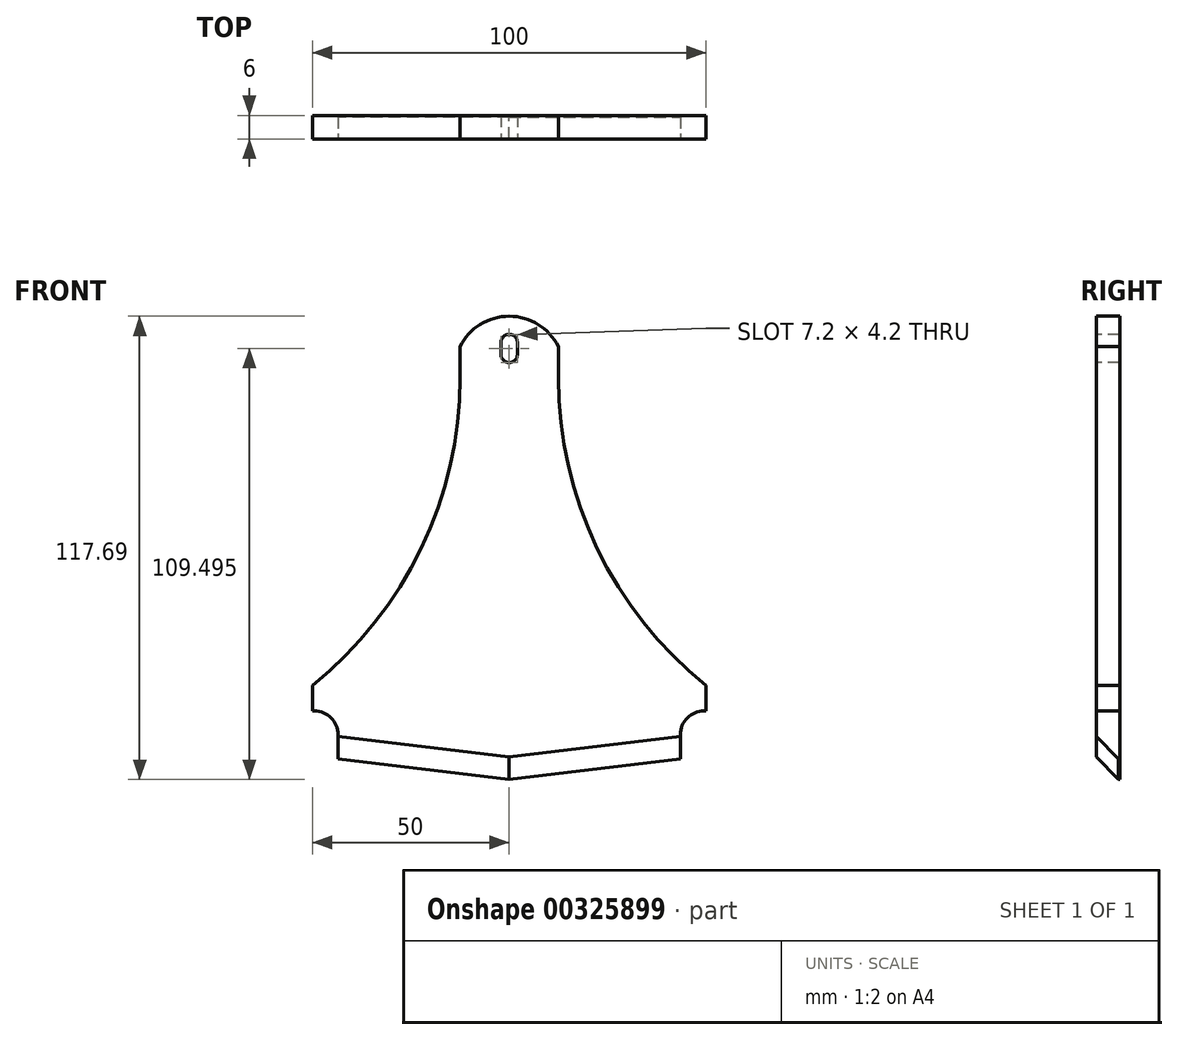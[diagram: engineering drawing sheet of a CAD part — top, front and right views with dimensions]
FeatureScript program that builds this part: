
annotation { "Feature Type Name" : "Feature", "Feature Type Description" : "" }
export const myFeature = defineFeature(function(context is Context, id is Id, definition is map)
    precondition{}
    {
        {
            var Q0;
            Q0=qCreatedBy(makeId("Front.planeOp"),FACE);
            var sketch = newSketch(context, id + "F0", { "sketchPlane" : qUnion([Q0])});
            skLineSegment(sketch, "E0", {"start": v(0, -15.28) * mm, "end": v(-43.5, -10.06) * mm});
            skLineSegment(sketch, "E1", {"start": v(0, -15.28) * mm, "end": v(0, 102.4) * mm});
            skLineSegment(sketch, "E2", {"start": v(-43.5, -10.06) * mm, "end": v(-43.5, 2.1) * mm});
            skCircle(sketch, "E3", {"center": v(0, 88.4) * mm, "radius": 14 * mm});
            skLineSegment(sketch, "E4", {"start": v(-43.5, 2.1) * mm, "end": v(-50, 2.1) * mm});
            skPoint(sketch, "E5", {"position": v(0, 102.4) * mm});
            skLineSegment(sketch, "E6", {"start": v(-12.5, 94.71) * mm, "end": v(-12.5, 8.6) * mm});
            skLineSegment(sketch, "E7", {"start": v(-50, 2.1) * mm, "end": v(-50, 8.6) * mm});
            skLineSegment(sketch, "E8", {"start": v(-50, 8.6) * mm, "end": v(-12.5, 8.6) * mm});
            skCircle(sketch, "E9", {"center": v(0, 95.71) * mm, "radius": 2.1 * mm});
            skCircle(sketch, "E10", {"center": v(0, 92.71) * mm, "radius": 2.1 * mm});
            skLineSegment(sketch, "E11", {"start": v(-2.1, 95.71) * mm, "end": v(-2.1, 92.71) * mm});
            skSolve(sketch);
        }
        {
            var Q0;
            {var subQ6=sQuery(id+"F0.wireOp",EDGE,"E0");Q0=makeQuery(id+"F0.imprint","IMPRINT",FACE,{"disambiguationData":[TD([[makeQuery(id+"F0.imprint","IMPRINT",EDGE,{"derivedFrom":subQ6}),-1.0]])]});}
            var Q1;
            {var subQ7=sQuery(id+"F0.wireOp",EDGE,"E11");Q1=makeQuery(id+"F0.imprint","IMPRINT",FACE,{"disambiguationData":[TD([[makeQuery(id+"F0.imprint","IMPRINT",EDGE,{"derivedFrom":subQ7}),-1.0]])]});}
            extrude(context, id + "F1", {"entities" : qUnion([Q0, Q1]), "oppositeDirection" : true, "depth" : 6 * mm});
        }
        {
            var Q0;
            Q0=makeQuery(id+"F1.opExtrude","SWEPT_EDGE",EDGE,{"disambiguationData":[OSD([sQuery(id+"F0.wireOp",EDGE,"E2"),sQuery(id+"F0.wireOp",EDGE,"E4")])]});
            fillet(context, id + "F2", {"entities" : qUnion([Q0]), "radius" : 6 * mm, "tangentPropagation" : true, "allowEdgeOverflow" : false});
        }
        {
            var Q0;
            Q0=makeQuery(id+"F1.opExtrude","CAP_EDGE",EDGE,{"disambiguationData":[OSD([sQuery(id+"F0.wireOp",EDGE,"E0")])],"isStart":true});
            chamfer(context, id + "F3", {"entities" : qUnion([Q0]), "chamferType" : ChamferType.TWO_OFFSETS, "width1" : 5.64 * mm, "oppositeDirection" : true, "width2" : 5.6 * mm, "tangentPropagation" : true});
        }
        {
            var Q0;
            Q0=makeQuery(id+"F1.opExtrude","SWEPT_EDGE",EDGE,{"disambiguationData":[OSD([sQuery(id+"F0.wireOp",EDGE,"E6"),sQuery(id+"F0.wireOp",EDGE,"E8")])]});
            fillet(context, id + "F4", {"entities" : qUnion([Q0]), "radius" : 100 * mm, "tangentPropagation" : true, "allowEdgeOverflow" : false});
        }
        {
            var Q0;
            Q0=makeQuery(id+"F1.opExtrude","SWEPT_BODY",BODY,{"disambiguationData":[OSD([sQuery(id+"F0.wireOp",EDGE,"E0"),sQuery(id+"F0.wireOp",EDGE,"E1"),sQuery(id+"F0.wireOp",EDGE,"E2"),sQuery(id+"F0.wireOp",EDGE,"E3"),sQuery(id+"F0.wireOp",EDGE,"E4"),sQuery(id+"F0.wireOp",EDGE,"E6"),sQuery(id+"F0.wireOp",EDGE,"E7"),sQuery(id+"F0.wireOp",EDGE,"E8"),sQuery(id+"F0.wireOp",EDGE,"E9"),sQuery(id+"F0.wireOp",EDGE,"E10"),sQuery(id+"F0.wireOp",EDGE,"E11")])]});
            var Q1;
            Q1=qCreatedBy(makeId("Right.planeOp"),FACE);
            mirror(context, id + "F5", {"operationType" : NewBodyOperationType.ADD, "entities" : qUnion([Q0]), "mirrorPlane" : qUnion([Q1])});
        }
    });
